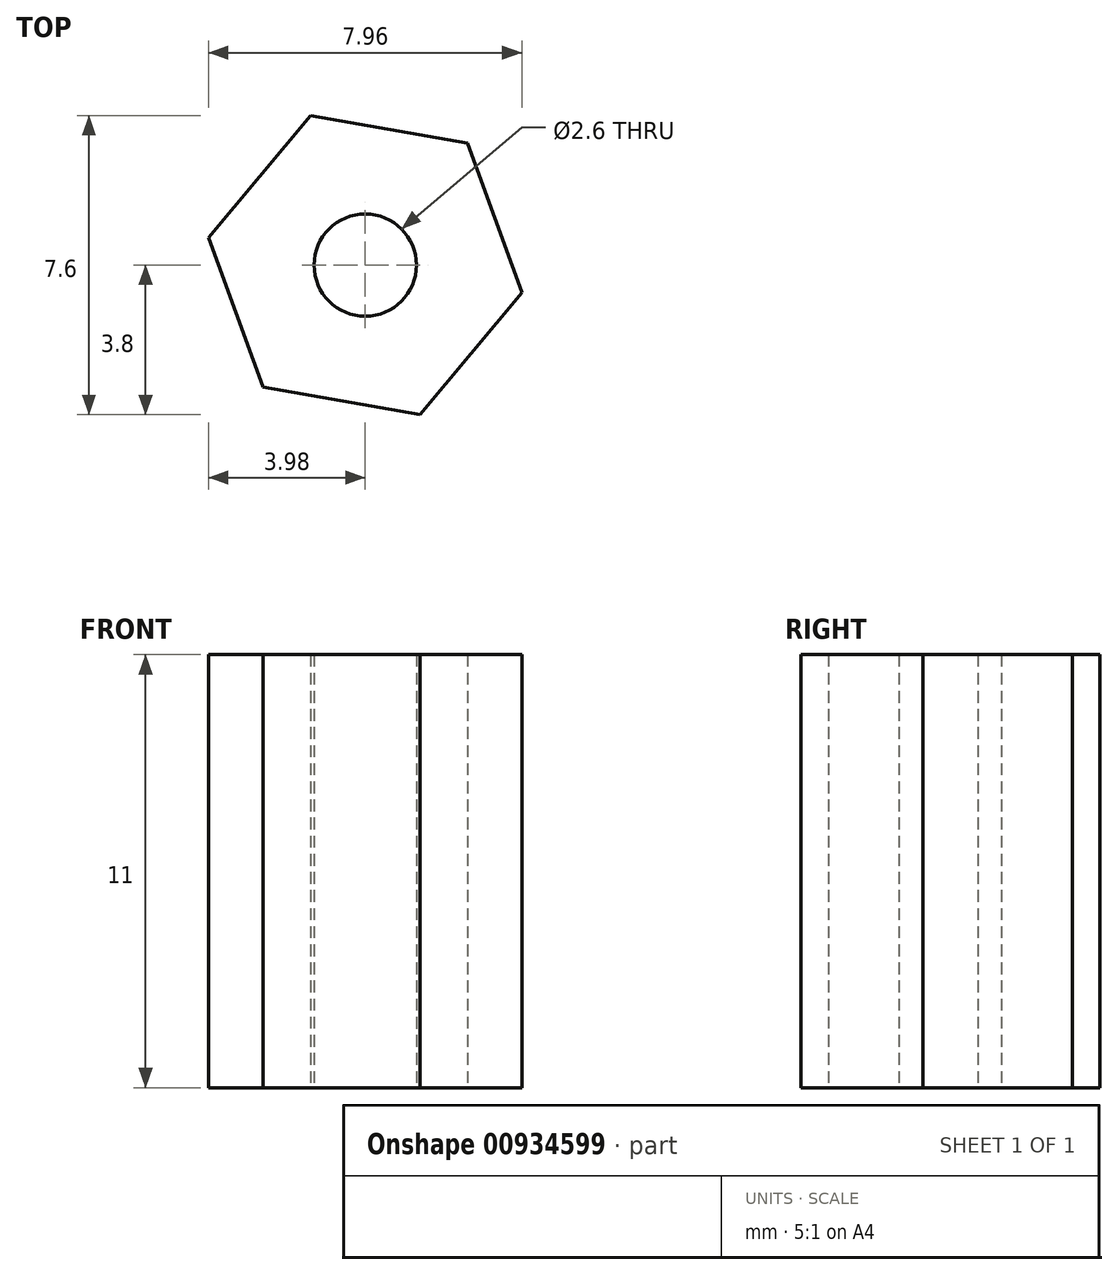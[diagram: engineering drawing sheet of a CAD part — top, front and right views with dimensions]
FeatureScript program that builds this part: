
annotation { "Feature Type Name" : "Feature", "Feature Type Description" : "" }
export const myFeature = defineFeature(function(context is Context, id is Id, definition is map)
    precondition{}
    {
        {
            var Q0;
            Q0=qCreatedBy(makeId("Top.planeOp"),FACE);
            var sketch = newSketch(context, id + "F0", { "sketchPlane" : qUnion([Q0])});
            skCircle(sketch, "E0", {"center": v(0, 0) * mm, "radius": 1.3 * mm});
            skCircle(sketch, "E1.cCircle", {"center": v(0, 0) * mm, "radius": 3.5 * mm, "construction": true});
            skLineSegment(sketch, "E1.0", {"start": v(3.98, -0.7) * mm, "end": v(1.39, -3.8) * mm});
            skLineSegment(sketch, "E1.1", {"start": v(1.39, -3.8) * mm, "end": v(-2.6, -3.1) * mm});
            skLineSegment(sketch, "E1.2", {"start": v(-2.6, -3.1) * mm, "end": v(-3.98, 0.7) * mm});
            skLineSegment(sketch, "E1.3", {"start": v(-3.98, 0.7) * mm, "end": v(-1.39, 3.8) * mm});
            skLineSegment(sketch, "E1.4", {"start": v(-1.39, 3.8) * mm, "end": v(2.6, 3.1) * mm});
            skLineSegment(sketch, "E1.5", {"start": v(2.6, 3.1) * mm, "end": v(3.98, -0.7) * mm});
            skPoint(sketch, "E1.0.midPoint", {"position": v(2.68, -2.25) * mm});
            skSolve(sketch);
        }
        {
            var Q0;
            Q0 = qSketchRegion(id + "F0", true);
            extrude(context, id + "F1", {"entities" : qUnion([Q0]), "depth" : 11 * mm, "offsetDistance" : 25 * mm});
        }
    });
